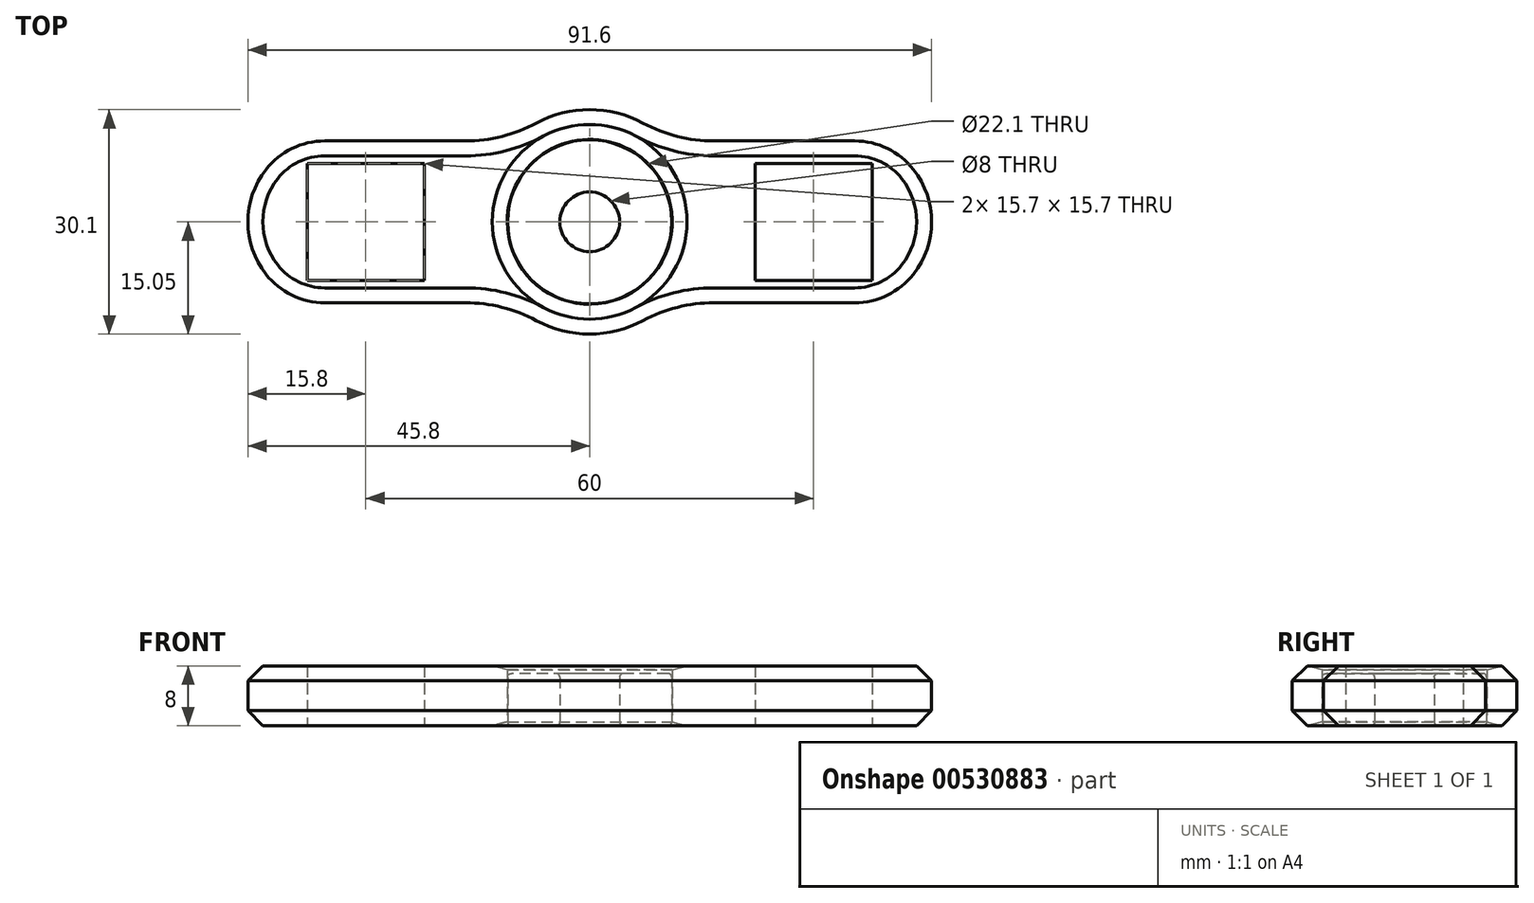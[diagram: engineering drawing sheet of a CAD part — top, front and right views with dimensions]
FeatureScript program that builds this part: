
annotation { "Feature Type Name" : "Feature", "Feature Type Description" : "" }
export const myFeature = defineFeature(function(context is Context, id is Id, definition is map)
    precondition{}
    {
        {
            var Q0;
            Q0=qCreatedBy(makeId("Top.planeOp"),FACE);
            var sketch = newSketch(context, id + "F0", { "sketchPlane" : qUnion([Q0])});
            skCircle(sketch, "E0", {"center": v(0, 0) * mm, "radius": 11 * mm});
            skCircle(sketch, "E1", {"center": v(0, 0) * mm, "radius": 4 * mm});
            skSolve(sketch);
        }
        {
            var Q0;
            Q0=makeQuery(id+"F0.imprint","IMPRINT",FACE,{"disambiguationData":[TD([[makeQuery(id+"F0.imprint","IMPRINT",EDGE,{"derivedFrom":sQuery(id+"F0.wireOp",EDGE,"E0")}),1.0]])]});
            extrude(context, id + "F1", {"entities" : qUnion([Q0]), "depth" : 7 * mm, "offsetDistance" : 25 * mm});
        }
        {
            var Q0;
            Q0=makeQuery(id+"F1.opExtrude","CAP_FACE",FACE,{"disambiguationData":[OSD([sQuery(id+"F0.wireOp",EDGE,"E0"),sQuery(id+"F0.wireOp",EDGE,"E1")])],"isStart":true});
            var sketch = newSketch(context, id + "F2", { "sketchPlane" : qUnion([Q0])});
            skCircle(sketch, "E2.0", {"center": v(0, 0) * mm, "radius": 11.05 * mm});
            skCircle(sketch, "E3.0", {"center": v(0, 0) * mm, "radius": 15.05 * mm});
            skLineSegment(sketch, "E4", {"start": v(0, 0) * mm, "end": v(-30, 0) * mm, "construction": true});
            skLineSegment(sketch, "E5.bottom", {"start": v(-37.85, -7.85) * mm, "end": v(-22.15, -7.85) * mm});
            skLineSegment(sketch, "E5.top", {"start": v(-37.85, 7.85) * mm, "end": v(-22.15, 7.85) * mm});
            skLineSegment(sketch, "E5.left", {"start": v(-37.85, -7.85) * mm, "end": v(-37.85, 7.85) * mm});
            skLineSegment(sketch, "E5.right", {"start": v(-22.15, -7.85) * mm, "end": v(-22.15, 7.85) * mm});
            skPoint(sketch, "E5.middle", {"position": v(-30, 0) * mm});
            skCircle(sketch, "E6", {"center": v(0, 0) * mm, "radius": 50 * mm, "construction": true});
            skLineSegment(sketch, "E7", {"start": v(-30, 0) * mm, "end": v(-45.8, 0) * mm, "construction": true});
            skLineSegment(sketch, "E8", {"start": v(-37.85, 7.85) * mm, "end": v(-37.85, 10.85) * mm, "construction": true});
            skLineSegment(sketch, "E9.0", {"start": v(-23, 10.85) * mm, "end": v(-37.85, 10.85) * mm});
            skLineSegment(sketch, "E9.1", {"start": v(0, 10.85) * mm, "end": v(-2.1, 10.85) * mm, "construction": true});
            skLineSegment(sketch, "E10.trimOffspring", {"start": v(-10.43, 10.85) * mm, "end": v(-23, 10.85) * mm});
            skLineSegment(sketch, "E11.MirrorCS", {"start": v(-10.43, -10.85) * mm, "end": v(-23, -10.85) * mm});
            skLineSegment(sketch, "E12.MirrorCS", {"start": v(-23, -10.85) * mm, "end": v(-37.85, -10.85) * mm});
            skArc(sketch, "E13", {"start": v(-37.85, 10.85) * mm, "mid": v(-45.8, 0) * mm, "end": v(-37.85, -10.85) * mm});
            skLineSegment(sketch, "E14.1.0", {"start": v(37.85, 7.85) * mm, "end": v(22.15, 7.85) * mm});
            skLineSegment(sketch, "E14.1.1", {"start": v(22.15, 7.85) * mm, "end": v(22.15, -7.85) * mm});
            skLineSegment(sketch, "E14.1.2", {"start": v(37.85, -7.85) * mm, "end": v(22.15, -7.85) * mm});
            skLineSegment(sketch, "E14.1.3", {"start": v(10.43, -10.85) * mm, "end": v(23, -10.85) * mm});
            skLineSegment(sketch, "E14.1.4", {"start": v(23, -10.85) * mm, "end": v(37.85, -10.85) * mm});
            skLineSegment(sketch, "E14.1.5", {"start": v(37.85, 7.85) * mm, "end": v(37.85, -7.85) * mm});
            skArc(sketch, "E14.1.6", {"start": v(37.85, -10.85) * mm, "mid": v(45.8, 0) * mm, "end": v(37.85, 10.85) * mm});
            skLineSegment(sketch, "E14.1.7", {"start": v(23, 10.85) * mm, "end": v(37.85, 10.85) * mm});
            skLineSegment(sketch, "E14.1.8", {"start": v(10.43, 10.85) * mm, "end": v(23, 10.85) * mm});
            skCircle(sketch, "E15", {"center": v(0, 0) * mm, "radius": 39.37 * mm, "construction": true});
            skSolve(sketch);
        }
        {
            var Q0;
            Q0=makeQuery(id+"F1.opExtrude","CAP_FACE",FACE,{"disambiguationData":[OSD([sQuery(id+"F0.wireOp",EDGE,"E0"),sQuery(id+"F0.wireOp",EDGE,"E1")])],"isStart":true});
            var Q1;
            Q1=makeQuery(id+"F1.opExtrude","CAP_FACE",FACE,{"disambiguationData":[OSD([sQuery(id+"F0.wireOp",EDGE,"E0"),sQuery(id+"F0.wireOp",EDGE,"E1")])],"isStart":false});
            fillet(context, id + "F3", {"entities" : qUnion([Q0, Q1]), "radius" : .5 * mm, "tangentPropagation" : true, "allowEdgeOverflow" : false});
        }
        {
            var Q0;
            {var subQ5=sQuery(id+"F2.wireOp",EDGE,"E14.2.0");Q0=makeQuery(id+"F2.imprint","IMPRINT",FACE,{"disambiguationData":[TD([[makeQuery(id+"F2.imprint","IMPRINT",EDGE,{"derivedFrom":subQ5}),-1.0]])]});}
            var Q1;
            Q1=makeQuery(id+"F2.imprint","IMPRINT",FACE,{"disambiguationData":[TD([[makeQuery(id+"F2.imprint","IMPRINT",EDGE,{"derivedFrom":sQuery(id+"F2.wireOp",EDGE,"E2.0")}),-1.0]])]});
            var Q2;
            {var subQ6=sQuery(id+"F2.wireOp",EDGE,"E14.1.0");Q2=makeQuery(id+"F2.imprint","IMPRINT",FACE,{"disambiguationData":[TD([[makeQuery(id+"F2.imprint","IMPRINT",EDGE,{"derivedFrom":subQ6}),-1.0]])]});}
            var Q3;
            {var subQ5=sQuery(id+"F2.wireOp",EDGE,"E5.bottom");Q3=makeQuery(id+"F2.imprint","IMPRINT",FACE,{"disambiguationData":[TD([[makeQuery(id+"F2.imprint","IMPRINT",EDGE,{"derivedFrom":subQ5}),-1.0]])]});}
            extrude(context, id + "F4", {"entities" : qUnion([Q0, Q1, Q2, Q3]), "oppositeDirection" : true, "depth" : 8 * mm, "offsetDistance" : 25 * mm});
        }
        {
            var Q0;
            Q0=makeQuery(id+"F4.opExtrude","SWEPT_EDGE",EDGE,{"disambiguationData":[OSD([sQuery(id+"F2.wireOp",EDGE,"E3.0"),sQuery(id+"F2.wireOp",EDGE,"E14.2.3")])]});
            var Q1;
            Q1=makeQuery(id+"F4.opExtrude","SWEPT_EDGE",EDGE,{"disambiguationData":[OSD([sQuery(id+"F2.wireOp",EDGE,"E3.0"),sQuery(id+"F2.wireOp",EDGE,"E14.1.8")])]});
            var Q2;
            Q2=makeQuery(id+"F4.opExtrude","SWEPT_EDGE",EDGE,{"disambiguationData":[OSD([sQuery(id+"F2.wireOp",EDGE,"E3.0"),sQuery(id+"F2.wireOp",EDGE,"E14.2.8")])]});
            var Q3;
            Q3=makeQuery(id+"F4.opExtrude","SWEPT_EDGE",EDGE,{"disambiguationData":[OSD([sQuery(id+"F2.wireOp",EDGE,"E3.0"),sQuery(id+"F2.wireOp",EDGE,"E10.trimOffspring")])]});
            var Q4;
            Q4=makeQuery(id+"F4.opExtrude","SWEPT_EDGE",EDGE,{"disambiguationData":[OSD([sQuery(id+"F2.wireOp",EDGE,"E3.0"),sQuery(id+"F2.wireOp",EDGE,"E11.MirrorCS")])]});
            var Q5;
            Q5=makeQuery(id+"F4.opExtrude","SWEPT_EDGE",EDGE,{"disambiguationData":[OSD([sQuery(id+"F2.wireOp",EDGE,"E3.0"),sQuery(id+"F2.wireOp",EDGE,"E14.1.3")])]});
            fillet(context, id + "F5", {"entities" : qUnion([Q0, Q1, Q2, Q3, Q4, Q5]), "radius" : 20 * mm, "tangentPropagation" : true, "allowEdgeOverflow" : false});
        }
        {
            var Q0;
            Q0=makeQuery(id+"F4.opExtrude","SWEPT_EDGE",EDGE,{"disambiguationData":[OSD([sQuery(id+"F2.wireOp",EDGE,"E14.2.4"),sQuery(id+"F2.wireOp",EDGE,"E14.2.6")])]});
            var Q1;
            Q1=makeQuery(id+"F4.opExtrude","SWEPT_EDGE",EDGE,{"disambiguationData":[OSD([sQuery(id+"F2.wireOp",EDGE,"E14.2.6"),sQuery(id+"F2.wireOp",EDGE,"E14.2.7")])]});
            var Q2;
            Q2=makeQuery(id+"F4.opExtrude","SWEPT_EDGE",EDGE,{"disambiguationData":[OSD([sQuery(id+"F2.wireOp",EDGE,"E9.0"),sQuery(id+"F2.wireOp",EDGE,"E13")])]});
            var Q3;
            Q3=makeQuery(id+"F4.opExtrude","SWEPT_EDGE",EDGE,{"disambiguationData":[OSD([sQuery(id+"F2.wireOp",EDGE,"E12.MirrorCS"),sQuery(id+"F2.wireOp",EDGE,"E13")])]});
            var Q4;
            Q4=makeQuery(id+"F4.opExtrude","SWEPT_EDGE",EDGE,{"disambiguationData":[OSD([sQuery(id+"F2.wireOp",EDGE,"E14.1.4"),sQuery(id+"F2.wireOp",EDGE,"E14.1.6")])]});
            var Q5;
            Q5=makeQuery(id+"F4.opExtrude","SWEPT_EDGE",EDGE,{"disambiguationData":[OSD([sQuery(id+"F2.wireOp",EDGE,"E14.1.6"),sQuery(id+"F2.wireOp",EDGE,"E14.1.7")])]});
            fillet(context, id + "F6", {"entities" : qUnion([Q0, Q1, Q2, Q3, Q4, Q5]), "radius" : 10 * mm, "tangentPropagation" : true, "allowEdgeOverflow" : false});
        }
        {
            var Q0;
            Q0=makeQuery(id+"F4.opExtrude","CAP_EDGE",EDGE,{"disambiguationData":[OSD([sQuery(id+"F2.wireOp",EDGE,"E14.2.6")])],"isStart":false});
            var Q1;
            Q1=makeQuery(id+"F4.opExtrude","CAP_EDGE",EDGE,{"disambiguationData":[OSD([sQuery(id+"F2.wireOp",EDGE,"E14.1.6")])],"isStart":false});
            var Q2;
            {var subQ0=sQuery(id+"F2.wireOp",EDGE,"E13");var subQ1=sQuery(id+"F2.wireOp",EDGE,"E9.0");Q2=makeQuery(id+"F6.opFillet","BLEND_EDGE",EDGE,{"blendedFrom":[makeQuery(id+"F4.opExtrude","SWEPT_EDGE",EDGE,{"disambiguationData":[OSD([subQ1,subQ0])]}),makeQuery(id+"F4.opExtrude","CAP_FACE",FACE,{"disambiguationData":[OSD([sQuery(id+"F2.wireOp",EDGE,"E2.0"),sQuery(id+"F2.wireOp",EDGE,"E3.0"),sQuery(id+"F2.wireOp",EDGE,"E5.bottom"),sQuery(id+"F2.wireOp",EDGE,"E5.top"),sQuery(id+"F2.wireOp",EDGE,"E5.left"),sQuery(id+"F2.wireOp",EDGE,"E5.right"),subQ1,sQuery(id+"F2.wireOp",EDGE,"E10.trimOffspring"),sQuery(id+"F2.wireOp",EDGE,"E11.MirrorCS"),sQuery(id+"F2.wireOp",EDGE,"E12.MirrorCS"),subQ0,sQuery(id+"F2.wireOp",EDGE,"E14.1.0"),sQuery(id+"F2.wireOp",EDGE,"E14.1.1"),sQuery(id+"F2.wireOp",EDGE,"E14.1.2"),sQuery(id+"F2.wireOp",EDGE,"E14.1.3"),sQuery(id+"F2.wireOp",EDGE,"E14.1.4"),sQuery(id+"F2.wireOp",EDGE,"E14.1.5"),sQuery(id+"F2.wireOp",EDGE,"E14.1.6"),sQuery(id+"F2.wireOp",EDGE,"E14.1.7"),sQuery(id+"F2.wireOp",EDGE,"E14.1.8"),sQuery(id+"F2.wireOp",EDGE,"E14.2.0"),sQuery(id+"F2.wireOp",EDGE,"E14.2.1"),sQuery(id+"F2.wireOp",EDGE,"E14.2.2"),sQuery(id+"F2.wireOp",EDGE,"E14.2.3"),sQuery(id+"F2.wireOp",EDGE,"E14.2.4"),sQuery(id+"F2.wireOp",EDGE,"E14.2.5"),sQuery(id+"F2.wireOp",EDGE,"E14.2.6"),sQuery(id+"F2.wireOp",EDGE,"E14.2.7"),sQuery(id+"F2.wireOp",EDGE,"E14.2.8")])],"isStart":false})],"blendedInto":[makeQuery(id+"F4.opExtrude","CAP_FACE",FACE,{"disambiguationData":[OSD([sQuery(id+"F2.wireOp",EDGE,"E2.0"),sQuery(id+"F2.wireOp",EDGE,"E3.0"),sQuery(id+"F2.wireOp",EDGE,"E5.bottom"),sQuery(id+"F2.wireOp",EDGE,"E5.top"),sQuery(id+"F2.wireOp",EDGE,"E5.left"),sQuery(id+"F2.wireOp",EDGE,"E5.right"),subQ1,sQuery(id+"F2.wireOp",EDGE,"E10.trimOffspring"),sQuery(id+"F2.wireOp",EDGE,"E11.MirrorCS"),sQuery(id+"F2.wireOp",EDGE,"E12.MirrorCS"),subQ0,sQuery(id+"F2.wireOp",EDGE,"E14.1.0"),sQuery(id+"F2.wireOp",EDGE,"E14.1.1"),sQuery(id+"F2.wireOp",EDGE,"E14.1.2"),sQuery(id+"F2.wireOp",EDGE,"E14.1.3"),sQuery(id+"F2.wireOp",EDGE,"E14.1.4"),sQuery(id+"F2.wireOp",EDGE,"E14.1.5"),sQuery(id+"F2.wireOp",EDGE,"E14.1.6"),sQuery(id+"F2.wireOp",EDGE,"E14.1.7"),sQuery(id+"F2.wireOp",EDGE,"E14.1.8"),sQuery(id+"F2.wireOp",EDGE,"E14.2.0"),sQuery(id+"F2.wireOp",EDGE,"E14.2.1"),sQuery(id+"F2.wireOp",EDGE,"E14.2.2"),sQuery(id+"F2.wireOp",EDGE,"E14.2.3"),sQuery(id+"F2.wireOp",EDGE,"E14.2.4"),sQuery(id+"F2.wireOp",EDGE,"E14.2.5"),sQuery(id+"F2.wireOp",EDGE,"E14.2.6"),sQuery(id+"F2.wireOp",EDGE,"E14.2.7"),sQuery(id+"F2.wireOp",EDGE,"E14.2.8")])],"isStart":false})]});}
            var Q3;
            Q3=makeQuery(id+"F4.opExtrude","CAP_EDGE",EDGE,{"disambiguationData":[OSD([sQuery(id+"F2.wireOp",EDGE,"E14.2.6")])],"isStart":true});
            var Q4;
            Q4=makeQuery(id+"F4.opExtrude","CAP_EDGE",EDGE,{"disambiguationData":[OSD([sQuery(id+"F2.wireOp",EDGE,"E13")])],"isStart":true});
            var Q5;
            Q5=makeQuery(id+"F4.opExtrude","CAP_EDGE",EDGE,{"disambiguationData":[OSD([sQuery(id+"F2.wireOp",EDGE,"E14.1.6")])],"isStart":true});
            chamfer(context, id + "F7", {"entities" : qUnion([Q0, Q1, Q2, Q3, Q4, Q5]), "width" : 2 * mm, "tangentPropagation" : true});
        }
        {
            var Q0;
            Q0=makeQuery(id+"F4.opExtrude","CAP_EDGE",EDGE,{"disambiguationData":[OSD([sQuery(id+"F2.wireOp",EDGE,"E2.0")])],"isStart":false});
            chamfer(context, id + "F8", {"entities" : qUnion([Q0]), "chamferType" : ChamferType.TWO_OFFSETS, "width1" : 2 * mm, "oppositeDirection" : false, "width2" : .5 * mm, "tangentPropagation" : true});
        }
        {
            var Q0;
            Q0=makeQuery(id+"F4.opExtrude","CAP_EDGE",EDGE,{"disambiguationData":[OSD([sQuery(id+"F2.wireOp",EDGE,"E2.0")])],"isStart":true});
            chamfer(context, id + "F9", {"entities" : qUnion([Q0]), "chamferType" : ChamferType.TWO_OFFSETS, "width1" : .5 * mm, "oppositeDirection" : false, "width2" : 2 * mm, "tangentPropagation" : true});
        }
    });
